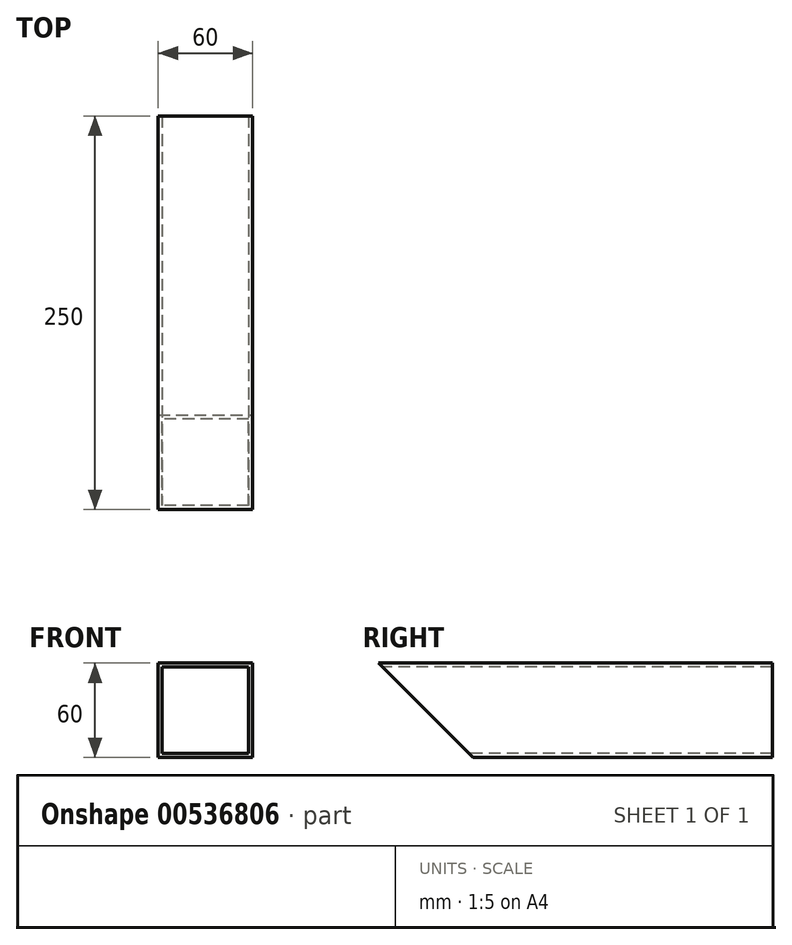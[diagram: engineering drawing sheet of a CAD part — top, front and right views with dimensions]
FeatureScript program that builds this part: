
annotation { "Feature Type Name" : "Feature", "Feature Type Description" : "" }
export const myFeature = defineFeature(function(context is Context, id is Id, definition is map)
    precondition{}
    {
        {
            var Q0;
            Q0=qCreatedBy(makeId("Front.planeOp"),FACE);
            var sketch = newSketch(context, id + "F0", { "sketchPlane" : qUnion([Q0])});
            skLineSegment(sketch, "E0.bottom", {"start": v(-30, -30) * mm, "end": v(30, -30) * mm});
            skLineSegment(sketch, "E0.top", {"start": v(-30, 30) * mm, "end": v(30, 30) * mm});
            skLineSegment(sketch, "E0.left", {"start": v(-30, -30) * mm, "end": v(-30, 30) * mm});
            skLineSegment(sketch, "E0.right", {"start": v(30, -30) * mm, "end": v(30, 30) * mm});
            skPoint(sketch, "E0.middle", {"position": v(0, 0) * mm});
            skLineSegment(sketch, "E1.bottom", {"start": v(-27.5, -27.5) * mm, "end": v(27.5, -27.5) * mm});
            skLineSegment(sketch, "E1.top", {"start": v(-27.5, 27.5) * mm, "end": v(27.5, 27.5) * mm});
            skLineSegment(sketch, "E1.left", {"start": v(-27.5, -27.5) * mm, "end": v(-27.5, 27.5) * mm});
            skLineSegment(sketch, "E1.right", {"start": v(27.5, -27.5) * mm, "end": v(27.5, 27.5) * mm});
            skSolve(sketch);
        }
        {
            var Q0;
            Q0 = qSketchRegion(id + "F0", true);
            extrude(context, id + "F1", {"entities" : qUnion([Q0]), "oppositeDirection" : true, "depth" : 250 * mm, "offsetDistance" : 25 * mm});
        }
        {
            var Q0;
            Q0=makeQuery(id+"F1.opExtrude","SWEPT_FACE",FACE,{"disambiguationData":[OSD([sQuery(id+"F0.wireOp",EDGE,"E0.right")])]});
            var sketch = newSketch(context, id + "F2", { "sketchPlane" : qUnion([Q0])});
            skLineSegment(sketch, "E2", {"start": v(0, 30) * mm, "end": v(82.46, -52.46) * mm});
            skSolve(sketch);
        }
        {
            var Q0;
            {var subQ1=sQuery(id+"F0.wireOp",EDGE,"E0.right");var subQ2=makeQuery(id+"F1.opExtrude","CAP_EDGE",EDGE,{"disambiguationData":[OSD([subQ1])],"isStart":true});Q0=makeQuery(id+"F2.imprint","IMPRINT",FACE,{"disambiguationData":[TD([[makeQuery(id+"F2.imprint","IMPRINT",EDGE,{"derivedFrom":subQ2}),-1.0]])]});}
            extrude(context, id + "F3", {"entities" : qUnion([Q0]), "operationType" : NewBodyOperationType.REMOVE, "oppositeDirection" : true, "depth" : 70 * mm, "offsetDistance" : 25 * mm});
        }
    });
